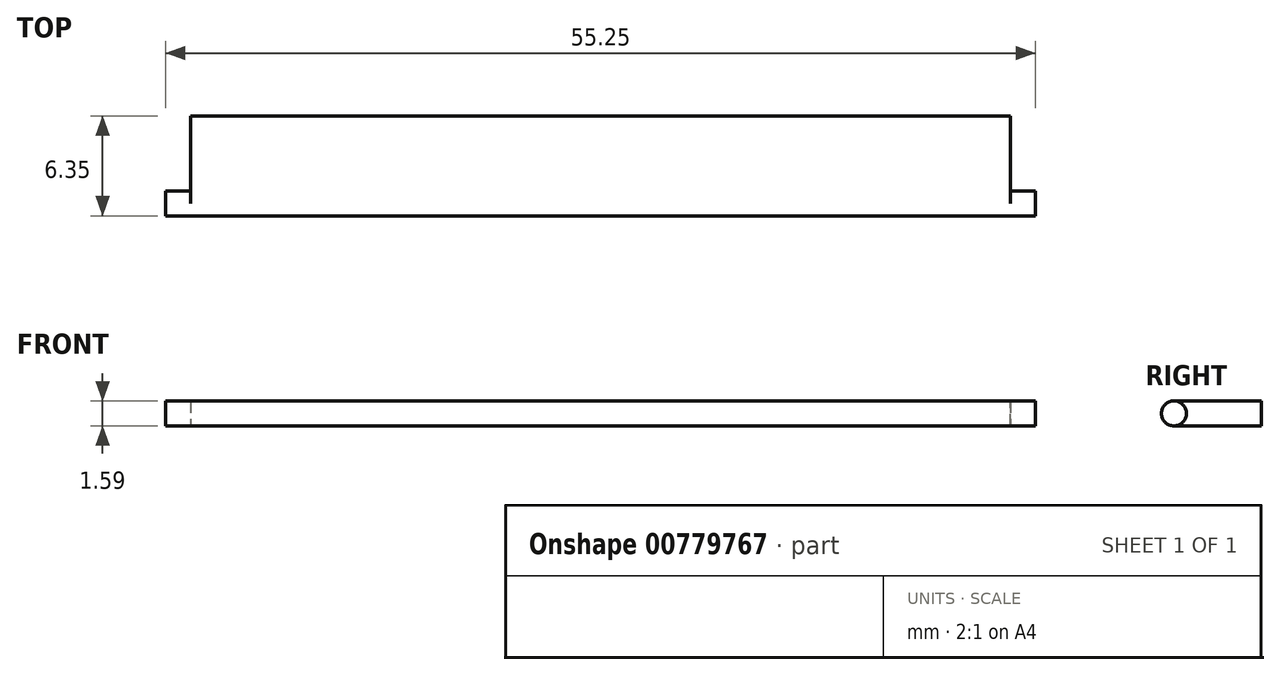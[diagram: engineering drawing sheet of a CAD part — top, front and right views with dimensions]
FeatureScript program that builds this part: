
annotation { "Feature Type Name" : "Feature", "Feature Type Description" : "" }
export const myFeature = defineFeature(function(context is Context, id is Id, definition is map)
    precondition{}
    {
        {
            var Q0;
            Q0=qCreatedBy(makeId("Top.planeOp"),FACE);
            var sketch = newSketch(context, id + "F0", { "sketchPlane" : qUnion([Q0])});
            skLineSegment(sketch, "E0.bottom", {"start": v(-13.98, -12.39) * mm, "end": v(38.09, -12.39) * mm});
            skLineSegment(sketch, "E0.top", {"start": v(-13.98, -18.74) * mm, "end": v(38.09, -18.74) * mm});
            skLineSegment(sketch, "E0.left", {"start": v(-13.98, -12.39) * mm, "end": v(-13.98, -18.74) * mm});
            skLineSegment(sketch, "E0.right", {"start": v(38.09, -12.39) * mm, "end": v(38.09, -18.74) * mm});
            skSolve(sketch);
        }
        {
            var Q0;
            Q0=makeQuery(id+"F0.imprint","IMPRINT",FACE,{"disambiguationData":[TD([[makeQuery(id+"F0.imprint","IMPRINT",EDGE,{"derivedFrom":sQuery(id+"F0.wireOp",EDGE,"E0.bottom")}),-1.0]])]});
            extrude(context, id + "F1", {"entities" : qUnion([Q0]), "depth" : 1.59 * mm, "offsetDistance" : 25.4 * mm});
        }
        {
            var Q0;
            Q0=makeQuery(id+"F1.opExtrude","SWEPT_FACE",FACE,{"disambiguationData":[OSD([sQuery(id+"F0.wireOp",EDGE,"E0.left")])]});
            var sketch = newSketch(context, id + "F2", { "sketchPlane" : qUnion([Q0])});
            skCircle(sketch, "E1", {"center": v(17.94, 0.8) * mm, "radius": 0.8 * mm});
            skPoint(sketch, "E1.centerSnap0", {"position": v(18.74, 0.8) * mm});
            skSolve(sketch);
        }
        {
            var Q0;
            {var subQ0=sQuery(id+"F2.wireOp",EDGE,"E1");var subQ1=sQuery(id+"F0.wireOp",EDGE,"E0.left");var subQ2=makeQuery(id+"F2.imprint","INTERSECT",VERTEX,{"derivedFrom":[makeQuery(id+"F1.opExtrude","CAP_EDGE",EDGE,{"disambiguationData":[OSD([subQ1])],"isStart":false}),subQ0]});Q0=makeQuery(id+"F2.imprint","IMPRINT",FACE,{"disambiguationData":[TD([[makeQuery(id+"F2.imprint","IMPRINT",EDGE,{"disambiguationData":[TD([[subQ2,-1.0]])],"derivedFrom":subQ0}),1.0]])]});}
            extrude(context, id + "F3", {"entities" : qUnion([Q0]), "operationType" : NewBodyOperationType.ADD, "depth" : 1.59 * mm, "offsetDistance" : 25.4 * mm});
        }
        {
            var Q0;
            Q0=makeQuery(id+"F1.opExtrude","SWEPT_FACE",FACE,{"disambiguationData":[OSD([sQuery(id+"F0.wireOp",EDGE,"E0.right")])]});
            var sketch = newSketch(context, id + "F4", { "sketchPlane" : qUnion([Q0])});
            skCircle(sketch, "E2", {"center": v(-17.94, 0.8) * mm, "radius": 0.8 * mm});
            skPoint(sketch, "E2.centerSnap0", {"position": v(-18.74, 0.8) * mm});
            skSolve(sketch);
        }
        {
            var Q0;
            {var subQ0=sQuery(id+"F4.wireOp",EDGE,"E2");var subQ1=sQuery(id+"F0.wireOp",EDGE,"E0.right");var subQ3=makeQuery(id+"F4.imprint","INTERSECT",VERTEX,{"derivedFrom":[makeQuery(id+"F1.opExtrude","CAP_EDGE",EDGE,{"disambiguationData":[OSD([subQ1])],"isStart":false}),subQ0]});Q0=makeQuery(id+"F4.imprint","IMPRINT",FACE,{"disambiguationData":[TD([[makeQuery(id+"F4.imprint","IMPRINT",EDGE,{"disambiguationData":[TD([[subQ3,1.0]])],"derivedFrom":subQ0}),1.0]])]});}
            extrude(context, id + "F5", {"entities" : qUnion([Q0]), "operationType" : NewBodyOperationType.ADD, "depth" : 1.59 * mm, "offsetDistance" : 25.4 * mm});
        }
        {
            var Q0;
            {var subQ0=sQuery(id+"F0.wireOp",EDGE,"E0.right");var subQ1=sQuery(id+"F0.wireOp",EDGE,"E0.top");var subQ2=makeQuery(id+"F1.opExtrude","SWEPT_FACE",FACE,{"disambiguationData":[OSD([subQ0])]});Q0=makeQuery(id+"F5.boolean.opBoolean","SPLIT",FACE,{"disambiguationData":[TD([makeQuery(id+"F1.opExtrude","CAP_FACE",FACE,{"disambiguationData":[OSD([sQuery(id+"F0.wireOp",EDGE,"E0.bottom"),subQ1,sQuery(id+"F0.wireOp",EDGE,"E0.left"),subQ0])],"isStart":false}),makeQuery(id+"F1.opExtrude","SWEPT_FACE",FACE,{"disambiguationData":[OSD([subQ1])]}),subQ2,makeQuery(id+"F5.opExtrude","SWEPT_FACE",FACE,{"disambiguationData":[OSD([sQuery(id+"F4.wireOp",EDGE,"E2")])]})])],"derivedFrom":subQ2});}
            var Q1;
            {var subQ0=sQuery(id+"F0.wireOp",EDGE,"E0.right");var subQ1=sQuery(id+"F0.wireOp",EDGE,"E0.top");var subQ2=makeQuery(id+"F1.opExtrude","SWEPT_FACE",FACE,{"disambiguationData":[OSD([subQ0])]});Q1=makeQuery(id+"F5.boolean.opBoolean","SPLIT",FACE,{"disambiguationData":[TD([makeQuery(id+"F1.opExtrude","CAP_FACE",FACE,{"disambiguationData":[OSD([sQuery(id+"F0.wireOp",EDGE,"E0.bottom"),subQ1,sQuery(id+"F0.wireOp",EDGE,"E0.left"),subQ0])],"isStart":true}),makeQuery(id+"F1.opExtrude","SWEPT_FACE",FACE,{"disambiguationData":[OSD([subQ1])]}),subQ2,makeQuery(id+"F5.opExtrude","SWEPT_FACE",FACE,{"disambiguationData":[OSD([sQuery(id+"F4.wireOp",EDGE,"E2")])]})])],"derivedFrom":subQ2});}
            extrude(context, id + "F6", {"entities" : qUnion([Q0, Q1]), "operationType" : NewBodyOperationType.REMOVE, "oppositeDirection" : true, "depth" : 52.07 * mm, "offsetDistance" : 25.4 * mm});
        }
    });
